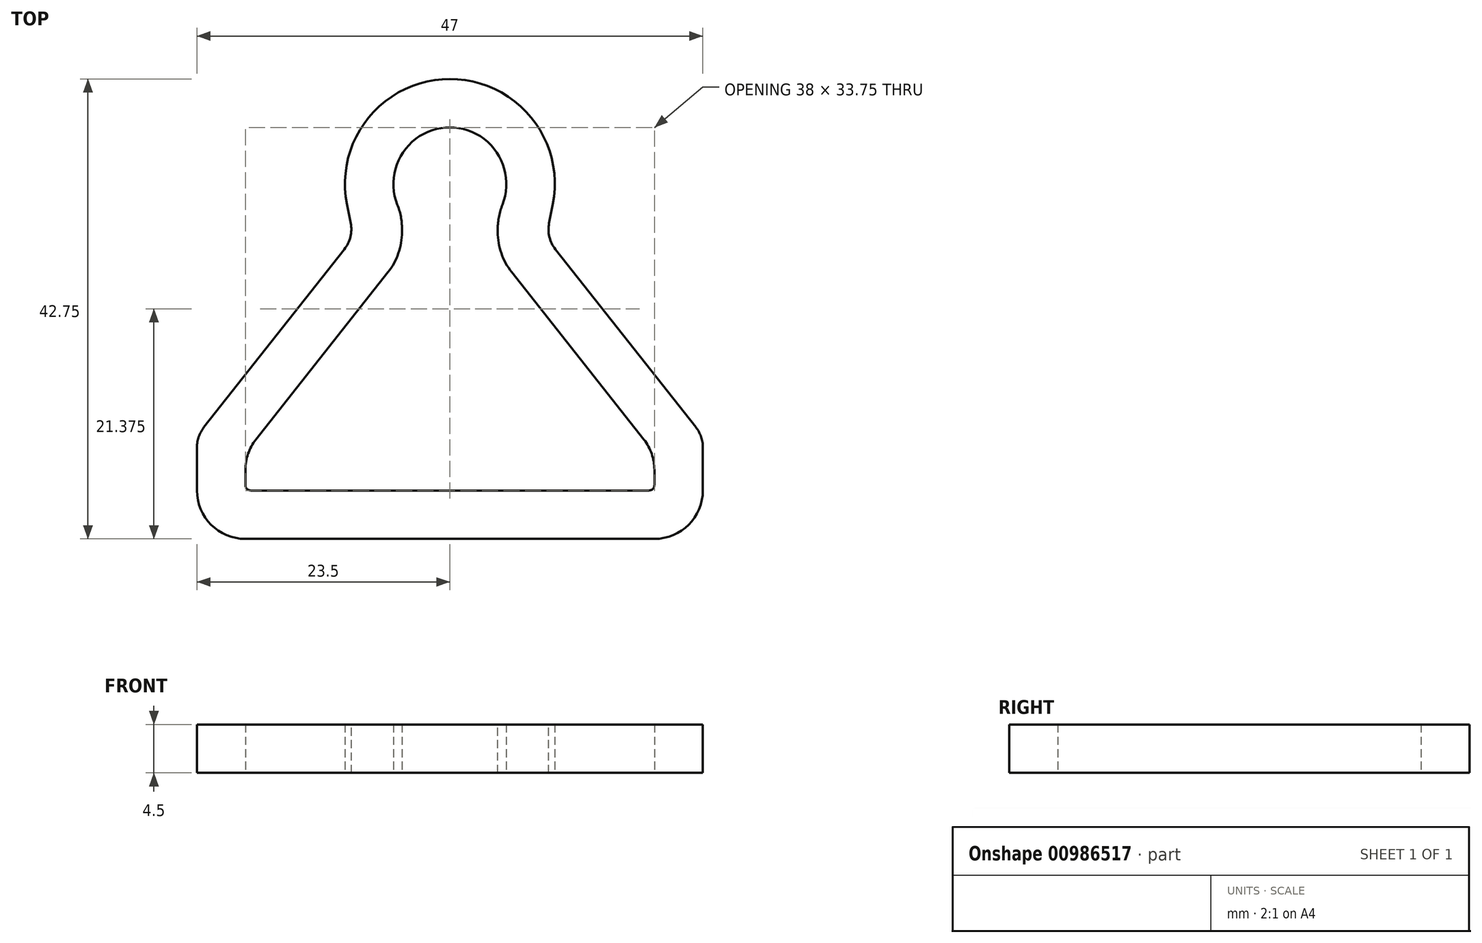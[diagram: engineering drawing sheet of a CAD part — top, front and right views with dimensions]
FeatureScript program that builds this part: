
annotation { "Feature Type Name" : "Feature", "Feature Type Description" : "" }
export const myFeature = defineFeature(function(context is Context, id is Id, definition is map)
    precondition{}
    {
        {
            var Q0;
            Q0=qCreatedBy(makeId("Top.planeOp"),FACE);
            var sketch = newSketch(context, id + "F0", { "sketchPlane" : qUnion([Q0])});
            skArc(sketch, "E0", {"start": v(4.45, -2.79) * mm, "mid": v(0, 5.25) * mm, "end": v(-4.45, -2.79) * mm});
            skLineSegment(sketch, "E1", {"start": v(-9.56, -1.9) * mm, "end": v(-8.95, -5) * mm});
            skLineSegment(sketch, "E2", {"start": v(-8.95, -5) * mm, "end": v(-23.5, -23.44) * mm});
            skLineSegment(sketch, "E3", {"start": v(-15.08, -5) * mm, "end": v(18.66, -5) * mm, "construction": true});
            skLineSegment(sketch, "E4", {"start": v(-4.45, -2.79) * mm, "end": v(-4.45, -6.56) * mm});
            skLineSegment(sketch, "E5", {"start": v(-4.45, -6.56) * mm, "end": v(-19, -25) * mm});
            skLineSegment(sketch, "E6.MirrorCS", {"start": v(4.45, -2.79) * mm, "end": v(4.45, -6.56) * mm});
            skLineSegment(sketch, "E7.MirrorCS", {"start": v(9.56, -1.9) * mm, "end": v(8.95, -5) * mm});
            skLineSegment(sketch, "E8.MirrorCS", {"start": v(8.95, -5) * mm, "end": v(23.5, -23.44) * mm});
            skLineSegment(sketch, "E9.MirrorCS", {"start": v(4.45, -6.56) * mm, "end": v(19, -25) * mm});
            skLineSegment(sketch, "E10", {"start": v(-19, -25) * mm, "end": v(-19, -28.5) * mm});
            skLineSegment(sketch, "E11", {"start": v(-19, -28.5) * mm, "end": v(19, -28.5) * mm});
            skLineSegment(sketch, "E12", {"start": v(19, -28.5) * mm, "end": v(19, -25) * mm});
            skLineSegment(sketch, "E13", {"start": v(-23.5, -23.44) * mm, "end": v(-23.5, -33) * mm});
            skLineSegment(sketch, "E14", {"start": v(-23.5, -33) * mm, "end": v(23.5, -33) * mm});
            skLineSegment(sketch, "E15", {"start": v(23.5, -33) * mm, "end": v(23.5, -23.44) * mm});
            skArc(sketch, "E16", {"start": v(9.56, -1.9) * mm, "mid": v(0, 9.75) * mm, "end": v(-9.56, -1.9) * mm});
            skSolve(sketch);
        }
        {
            var Q0;
            Q0=makeQuery(id+"F0.imprint","IMPRINT",FACE,{"disambiguationData":[TD([[makeQuery(id+"F0.imprint","IMPRINT",EDGE,{"derivedFrom":sQuery(id+"F0.wireOp",EDGE,"E0")}),-1.0]])]});
            extrude(context, id + "F1", {"entities" : qUnion([Q0]), "depth" : 4.5 * mm, "offsetDistance" : 25 * mm});
        }
        {
            var Q0;
            Q0=makeQuery(id+"F1.opExtrude","SWEPT_EDGE",EDGE,{"disambiguationData":[OSD([sQuery(id+"F0.wireOp",EDGE,"E5"),sQuery(id+"F0.wireOp",EDGE,"E10")])]});
            var Q1;
            Q1=makeQuery(id+"F1.opExtrude","SWEPT_EDGE",EDGE,{"disambiguationData":[OSD([sQuery(id+"F0.wireOp",EDGE,"E9.MirrorCS"),sQuery(id+"F0.wireOp",EDGE,"E12")])]});
            var Q2;
            Q2=makeQuery(id+"F1.opExtrude","SWEPT_EDGE",EDGE,{"disambiguationData":[OSD([sQuery(id+"F0.wireOp",EDGE,"E13"),sQuery(id+"F0.wireOp",EDGE,"E14")])]});
            var Q3;
            Q3=makeQuery(id+"F1.opExtrude","SWEPT_EDGE",EDGE,{"disambiguationData":[OSD([sQuery(id+"F0.wireOp",EDGE,"E14"),sQuery(id+"F0.wireOp",EDGE,"E15")])]});
            fillet(context, id + "F2", {"entities" : qUnion([Q0, Q1, Q2, Q3]), "radius" : 4.5 * mm, "tangentPropagation" : true, "allowEdgeOverflow" : false});
        }
        {
            var Q0;
            Q0=makeQuery(id+"F1.opExtrude","SWEPT_EDGE",EDGE,{"disambiguationData":[OSD([sQuery(id+"F0.wireOp",EDGE,"E1"),sQuery(id+"F0.wireOp",EDGE,"E2")])]});
            var Q1;
            Q1=makeQuery(id+"F1.opExtrude","SWEPT_EDGE",EDGE,{"disambiguationData":[OSD([sQuery(id+"F0.wireOp",EDGE,"E7.MirrorCS"),sQuery(id+"F0.wireOp",EDGE,"E8.MirrorCS")])]});
            var Q2;
            Q2=makeQuery(id+"F1.opExtrude","SWEPT_EDGE",EDGE,{"disambiguationData":[OSD([sQuery(id+"F0.wireOp",EDGE,"E8.MirrorCS"),sQuery(id+"F0.wireOp",EDGE,"E15")])]});
            var Q3;
            Q3=makeQuery(id+"F1.opExtrude","SWEPT_EDGE",EDGE,{"disambiguationData":[OSD([sQuery(id+"F0.wireOp",EDGE,"E2"),sQuery(id+"F0.wireOp",EDGE,"E13")])]});
            fillet(context, id + "F3", {"entities" : qUnion([Q0, Q1, Q2, Q3]), "radius" : 3 * mm, "tangentPropagation" : true, "allowEdgeOverflow" : false});
        }
        {
            var Q0;
            Q0=makeQuery(id+"F1.opExtrude","SWEPT_EDGE",EDGE,{"disambiguationData":[OSD([sQuery(id+"F0.wireOp",EDGE,"E10"),sQuery(id+"F0.wireOp",EDGE,"E11")])]});
            var Q1;
            Q1=makeQuery(id+"F1.opExtrude","SWEPT_EDGE",EDGE,{"disambiguationData":[OSD([sQuery(id+"F0.wireOp",EDGE,"E11"),sQuery(id+"F0.wireOp",EDGE,"E12")])]});
            fillet(context, id + "F4", {"entities" : qUnion([Q0, Q1]), "radius" : 0.5 * mm, "tangentPropagation" : true, "allowEdgeOverflow" : false});
        }
        {
            var Q0;
            Q0=makeQuery(id+"F1.opExtrude","SWEPT_EDGE",EDGE,{"disambiguationData":[OSD([sQuery(id+"F0.wireOp",EDGE,"E6.MirrorCS"),sQuery(id+"F0.wireOp",EDGE,"E9.MirrorCS")])]});
            var Q1;
            Q1=makeQuery(id+"F1.opExtrude","SWEPT_EDGE",EDGE,{"disambiguationData":[OSD([sQuery(id+"F0.wireOp",EDGE,"E4"),sQuery(id+"F0.wireOp",EDGE,"E5")])]});
            var Q2;
            Q2=makeQuery(id+"F1.opExtrude","SWEPT_EDGE",EDGE,{"disambiguationData":[OSD([sQuery(id+"F0.wireOp",EDGE,"E0"),sQuery(id+"F0.wireOp",EDGE,"E6.MirrorCS")])]});
            var Q3;
            Q3=makeQuery(id+"F1.opExtrude","SWEPT_EDGE",EDGE,{"disambiguationData":[OSD([sQuery(id+"F0.wireOp",EDGE,"E0"),sQuery(id+"F0.wireOp",EDGE,"E4")])]});
            fillet(context, id + "F5", {"entities" : qUnion([Q0, Q1, Q2, Q3]), "radius" : 6 * mm, "tangentPropagation" : true, "allowEdgeOverflow" : false});
        }
    });
